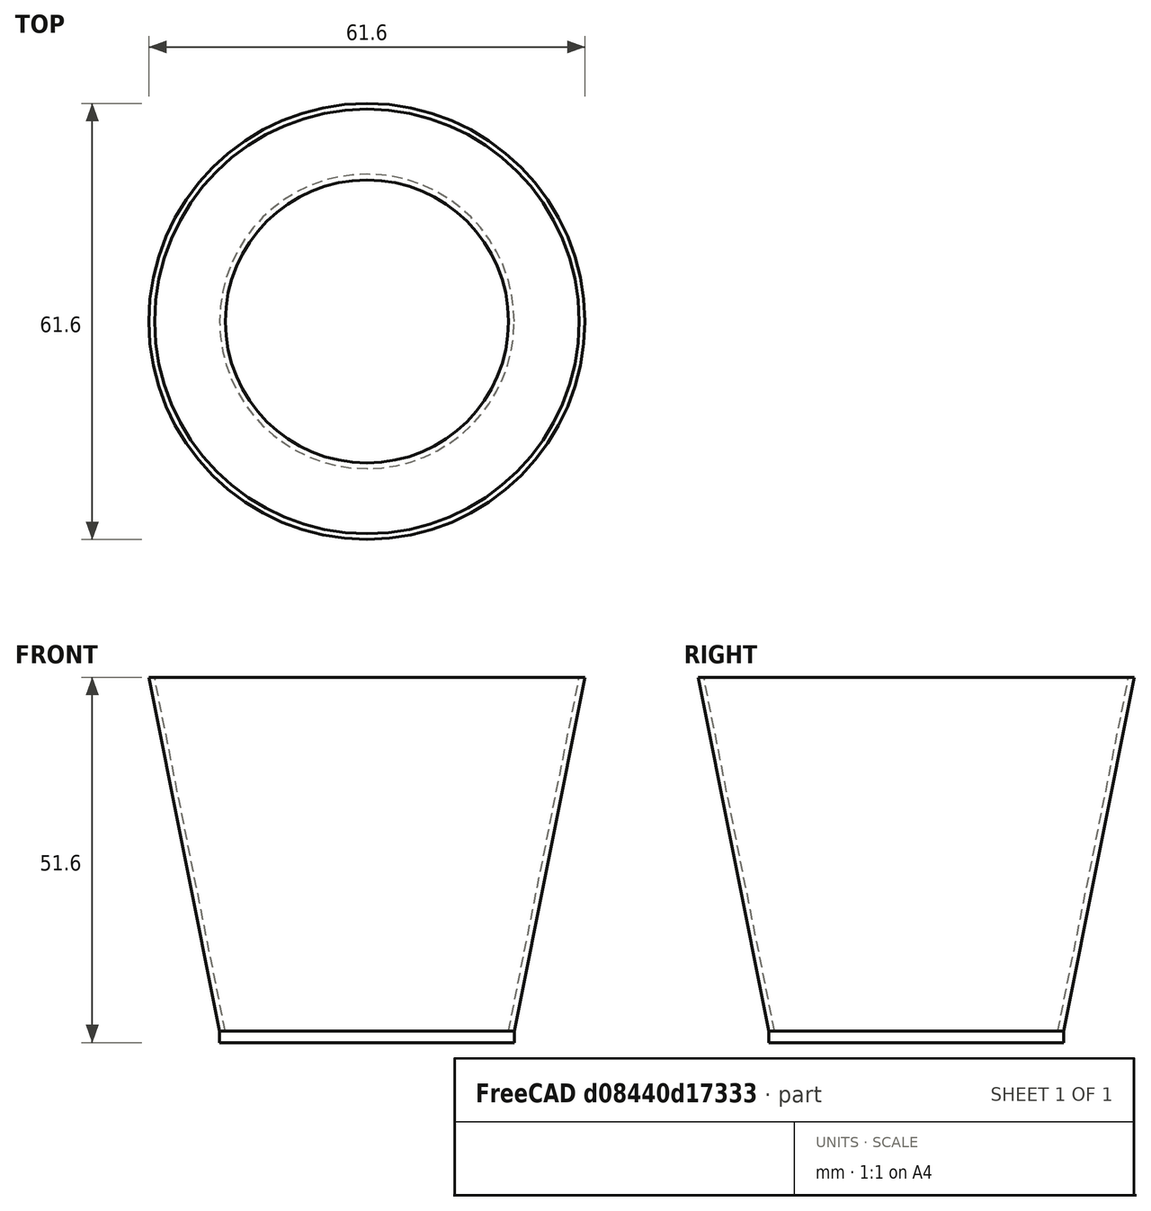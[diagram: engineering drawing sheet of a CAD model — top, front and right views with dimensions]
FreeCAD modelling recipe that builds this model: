
FCSTD DOCUMENT  (FreeCAD 0.20R29177 (Git))
Label: SmallCup100ml
License: All rights reserved
LicenseURL: http://en.wikipedia.org/wiki/All_rights_reserved
objects: Part::Cone×2, Sketcher::SketchObject×1, Part::Face×1, Part::Extrusion×1, Part::Cut×1, Part::Fuse×1
note: 7 computed .brp shape members not serialized (recipe doc carries the construction recipe); baked Part::Feature solids carry a one-line shape summary decoded from their .brp

FEATURE [Sketcher::SketchObject] Sketch
  FullyConstrained = true
  sketch-geometry (1):
    g0: Circle CenterX=0 CenterY=0 CenterZ=0 NormalX=0 NormalY=0 NormalZ=1 AngleXU=0 Radius=20.8
  constraints (2):
    c: Radius(g0) = 20.8
    c: Coincident(g0,g-1)
FEATURE [Part::Face] Face
  FaceMakerClass = Part::FaceMakerBullseye
  Sources = -> [Sketch]
FEATURE [Part::Extrusion] Extrude
  Base = -> Sketch
  Dir = (0,0,1)
  DirMode = 2
  FaceMakerClass = Part::FaceMakerBullseye
  LengthFwd = -1.6
  LengthRev = 0
  Solid = true
  Symmetric = false
FEATURE [Part::Cone] Cone
  Angle = 360
  AttacherType = Attacher::AttachEngine3D
  Height = 50
  Radius1 = 20.8
  Radius2 = 30.8
FEATURE [Part::Cone] Cone001
  Angle = 360
  AttacherType = Attacher::AttachEngine3D
  Height = 50
  Radius1 = 20
  Radius2 = 30
FEATURE [Part::Cut] Cut
  Base = -> Cone
  Tool = -> Cone001
FEATURE [Part::Fuse] Fusion
  Base = -> Extrude
  Tool = -> Cut
